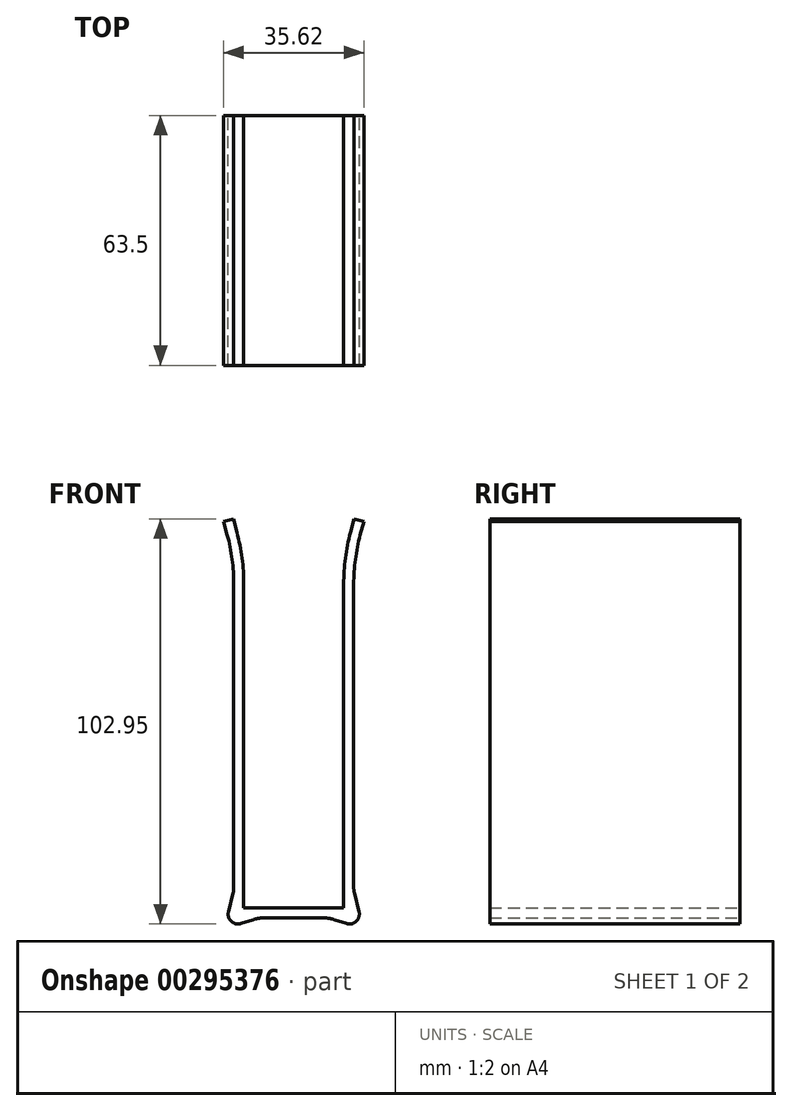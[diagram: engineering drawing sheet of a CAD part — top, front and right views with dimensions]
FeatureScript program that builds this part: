
annotation { "Feature Type Name" : "Feature", "Feature Type Description" : "" }
export const myFeature = defineFeature(function(context is Context, id is Id, definition is map)
    precondition{}
    {
        {
            var Q0;
            Q0=qCreatedBy(makeId("Front.planeOp"),FACE);
            var sketch = newSketch(context, id + "F0", { "sketchPlane" : qUnion([Q0])});
            skLineSegment(sketch, "E0", {"start": v(-12.7, 46.11) * mm, "end": v(-12.7, -36.1) * mm});
            skLineSegment(sketch, "E1", {"start": v(-12.7, -36.1) * mm, "end": v(0, -36.1) * mm});
            skLineSegment(sketch, "E2", {"start": v(-14.43, 59.26) * mm, "end": v(-15.36, 62.72) * mm});
            skPoint(sketch, "E3.visualSharp", {"position": v(-12.7, 52.8) * mm});
            skArc(sketch, "E3.filletArc", {"start": v(-12.7, 46.11) * mm, "mid": v(-13.13, 52.75) * mm, "end": v(-14.43, 59.26) * mm});
            skLineSegment(sketch, "E4.4", {"start": v(-16.88, 58.6) * mm, "end": v(-17.81, 62.06) * mm});
            skArc(sketch, "E4.5", {"start": v(-15.24, 46.11) * mm, "mid": v(-15.65, 52.41) * mm, "end": v(-16.88, 58.6) * mm});
            skLineSegment(sketch, "E4.6", {"start": v(-15.24, 46.11) * mm, "end": v(-15.24, -31.05) * mm});
            skLineSegment(sketch, "E4.7", {"start": v(-7.23, -38.64) * mm, "end": v(0, -38.64) * mm});
            skLineSegment(sketch, "E5", {"start": v(-17.81, 62.06) * mm, "end": v(-15.36, 62.72) * mm});
            skLineSegment(sketch, "E6", {"start": v(-15.4, -32.3) * mm, "end": v(-16.6, -37.07) * mm});
            skLineSegment(sketch, "E7", {"start": v(-13.34, -40.1) * mm, "end": v(-10.4, -39.14) * mm});
            skPoint(sketch, "E8.visualSharp", {"position": v(-17.71, -41.54) * mm});
            skArc(sketch, "E8.filletArc", {"start": v(-16.6, -37.07) * mm, "mid": v(-15.86, -39.55) * mm, "end": v(-13.34, -40.1) * mm});
            skPoint(sketch, "E9.newPointA", {"position": v(-15.24, -38.64) * mm});
            skPoint(sketch, "E9.newPointB", {"position": v(-15.24, -31.68) * mm});
            skArc(sketch, "E9.filletArc", {"start": v(-15.4, -32.3) * mm, "mid": v(-15.28, -31.68) * mm, "end": v(-15.24, -31.05) * mm});
            skPoint(sketch, "E10.newPointB", {"position": v(-8.06, -38.38) * mm});
            skArc(sketch, "E10.filletArc", {"start": v(-7.23, -38.64) * mm, "mid": v(-8.83, -38.76) * mm, "end": v(-10.4, -39.14) * mm});
            skLineSegment(sketch, "E11.MirrorCS", {"start": v(13.34, -40.1) * mm, "end": v(10.4, -39.14) * mm});
            skArc(sketch, "E12.MirrorCS", {"start": v(15.4, -32.3) * mm, "mid": v(15.28, -31.68) * mm, "end": v(15.24, -31.05) * mm});
            skArc(sketch, "E13.MirrorCS", {"start": v(7.23, -38.64) * mm, "mid": v(8.83, -38.76) * mm, "end": v(10.4, -39.14) * mm});
            skLineSegment(sketch, "E14.MirrorCS", {"start": v(15.4, -32.3) * mm, "end": v(16.6, -37.07) * mm});
            skArc(sketch, "E15.MirrorCS", {"start": v(16.6, -37.07) * mm, "mid": v(15.86, -39.55) * mm, "end": v(13.34, -40.1) * mm});
            skLineSegment(sketch, "E16.MirrorCS", {"start": v(17.81, 62.06) * mm, "end": v(15.36, 62.72) * mm});
            skLineSegment(sketch, "E17.MirrorCS", {"start": v(14.43, 59.26) * mm, "end": v(15.36, 62.72) * mm});
            skLineSegment(sketch, "E18.MirrorCS", {"start": v(16.88, 58.6) * mm, "end": v(17.81, 62.06) * mm});
            skArc(sketch, "E19.MirrorCS", {"start": v(15.24, 46.11) * mm, "mid": v(15.65, 52.41) * mm, "end": v(16.88, 58.6) * mm});
            skPoint(sketch, "E20.MirrorP", {"position": v(17.71, -41.54) * mm});
            skPoint(sketch, "E21.MirrorP", {"position": v(8.06, -38.38) * mm});
            skLineSegment(sketch, "E22.MirrorCS", {"start": v(7.23, -38.64) * mm, "end": v(0, -38.64) * mm});
            skPoint(sketch, "E23.MirrorP", {"position": v(15.24, -38.64) * mm});
            skPoint(sketch, "E24.MirrorP", {"position": v(15.24, -31.68) * mm});
            skArc(sketch, "E25.MirrorCS", {"start": v(12.7, 46.11) * mm, "mid": v(13.13, 52.75) * mm, "end": v(14.43, 59.26) * mm});
            skLineSegment(sketch, "E26.MirrorCS", {"start": v(12.7, 46.11) * mm, "end": v(12.7, -36.1) * mm});
            skPoint(sketch, "E27.MirrorP", {"position": v(12.7, 52.8) * mm});
            skLineSegment(sketch, "E28.MirrorCS", {"start": v(15.24, 46.11) * mm, "end": v(15.24, -31.05) * mm});
            skLineSegment(sketch, "E29.MirrorCS", {"start": v(12.7, -36.1) * mm, "end": v(0, -36.1) * mm});
            skSolve(sketch);
        }
        {
            var Q0;
            Q0=makeQuery(id+"F0.imprint","IMPRINT",FACE,{"disambiguationData":[TD([[makeQuery(id+"F0.imprint","IMPRINT",EDGE,{"derivedFrom":sQuery(id+"F0.wireOp",EDGE,"E0")}),-1.0]])]});
            extrude(context, id + "F1", {"entities" : qUnion([Q0]), "depth" : 63.5 * mm});
        }
    });
